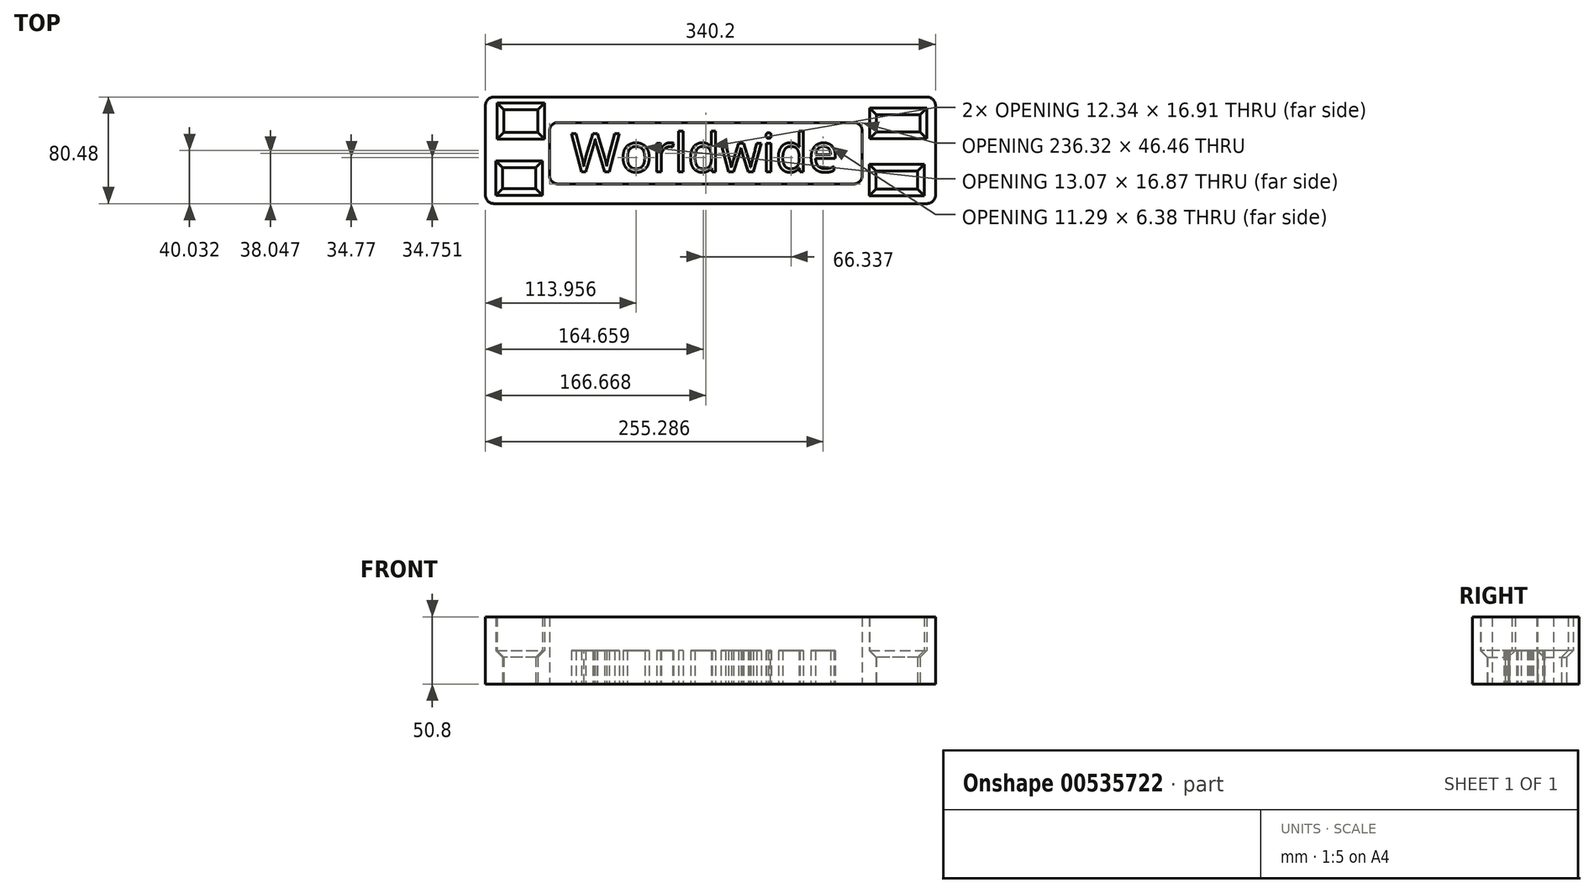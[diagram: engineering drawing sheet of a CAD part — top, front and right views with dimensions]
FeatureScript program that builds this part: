
annotation { "Feature Type Name" : "Feature", "Feature Type Description" : "" }
export const myFeature = defineFeature(function(context is Context, id is Id, definition is map)
    precondition{}
    {
        {
            var Q0;
            Q0=qCreatedBy(makeId("Top.planeOp"),FACE);
            var sketch = newSketch(context, id + "F0", { "sketchPlane" : qUnion([Q0])});
            skLineSegment(sketch, "E0.bottom", {"start": v(-163.75, 40.24) * mm, "end": v(163.75, 40.24) * mm});
            skLineSegment(sketch, "E0.top", {"start": v(-163.75, -40.24) * mm, "end": v(163.75, -40.24) * mm});
            skLineSegment(sketch, "E0.left", {"start": v(-170.1, 33.9) * mm, "end": v(-170.1, -33.9) * mm});
            skLineSegment(sketch, "E0.right", {"start": v(170.1, 33.9) * mm, "end": v(170.1, -33.9) * mm});
            skPoint(sketch, "E0.middle", {"position": v(0, 0) * mm});
            skPoint(sketch, "E1.visualSharp", {"position": v(-170.1, 40.24) * mm});
            skArc(sketch, "E1.filletArc", {"start": v(-163.75, 40.24) * mm, "mid": v(-168.24, 38.38) * mm, "end": v(-170.1, 33.9) * mm});
            skPoint(sketch, "E2.visualSharp", {"position": v(170.1, 40.24) * mm});
            skArc(sketch, "E2.filletArc", {"start": v(170.1, 33.9) * mm, "mid": v(168.24, 38.38) * mm, "end": v(163.75, 40.24) * mm});
            skPoint(sketch, "E3.visualSharp", {"position": v(-170.1, -40.24) * mm});
            skArc(sketch, "E3.filletArc", {"start": v(-170.1, -33.9) * mm, "mid": v(-168.24, -38.38) * mm, "end": v(-163.75, -40.24) * mm});
            skPoint(sketch, "E4.visualSharp", {"position": v(170.1, -40.24) * mm});
            skArc(sketch, "E4.filletArc", {"start": v(163.75, -40.24) * mm, "mid": v(168.24, -38.38) * mm, "end": v(170.1, -33.9) * mm});
            skLineSegment(sketch, "E5.bottom", {"start": v(0, 0) * mm, "end": v(0, 0) * mm});
            skLineSegment(sketch, "E5.top", {"start": v(0, 0) * mm, "end": v(0, 0) * mm});
            skLineSegment(sketch, "E5.left", {"start": v(0, 0) * mm, "end": v(0, 0) * mm});
            skLineSegment(sketch, "E5.right", {"start": v(0, 0) * mm, "end": v(0, 0) * mm});
            skLineSegment(sketch, "E6.bottom", {"start": v(108.38, 21.04) * mm, "end": v(-115.24, 21.04) * mm});
            skLineSegment(sketch, "E6.top", {"start": v(108.38, -25.42) * mm, "end": v(-115.24, -25.42) * mm});
            skLineSegment(sketch, "E6.left", {"start": v(114.73, 14.69) * mm, "end": v(114.73, -19.07) * mm});
            skLineSegment(sketch, "E6.right", {"start": v(-121.59, 14.69) * mm, "end": v(-121.59, -19.07) * mm});
            skPoint(sketch, "E7.visualSharp", {"position": v(114.73, 21.04) * mm});
            skArc(sketch, "E7.filletArc", {"start": v(114.73, 14.69) * mm, "mid": v(112.87, 19.18) * mm, "end": v(108.38, 21.04) * mm});
            skPoint(sketch, "E8.visualSharp", {"position": v(114.73, -25.42) * mm});
            skArc(sketch, "E8.filletArc", {"start": v(108.38, -25.42) * mm, "mid": v(112.87, -23.56) * mm, "end": v(114.73, -19.07) * mm});
            skPoint(sketch, "E9.visualSharp", {"position": v(-121.59, 21.04) * mm});
            skArc(sketch, "E9.filletArc", {"start": v(-115.24, 21.04) * mm, "mid": v(-119.73, 19.18) * mm, "end": v(-121.59, 14.69) * mm});
            skPoint(sketch, "E10.visualSharp", {"position": v(-121.59, -25.42) * mm});
            skArc(sketch, "E10.filletArc", {"start": v(-121.59, -19.07) * mm, "mid": v(-119.73, -23.56) * mm, "end": v(-115.24, -25.42) * mm});
            skLineSegment(sketch, "E11.bottom", {"start": v(158.53, 26.97) * mm, "end": v(125.6, 26.97) * mm});
            skLineSegment(sketch, "E11.top", {"start": v(158.53, 14.03) * mm, "end": v(125.6, 14.03) * mm});
            skLineSegment(sketch, "E11.left", {"start": v(158.53, 26.97) * mm, "end": v(158.53, 14.03) * mm});
            skLineSegment(sketch, "E11.right", {"start": v(125.6, 26.97) * mm, "end": v(125.6, 14.03) * mm});
            skLineSegment(sketch, "E12.bottom", {"start": v(156.44, -15.5) * mm, "end": v(125.26, -15.5) * mm});
            skLineSegment(sketch, "E12.top", {"start": v(156.44, -29.19) * mm, "end": v(125.26, -29.19) * mm});
            skLineSegment(sketch, "E12.left", {"start": v(156.44, -15.5) * mm, "end": v(156.44, -29.19) * mm});
            skLineSegment(sketch, "E12.right", {"start": v(125.26, -15.5) * mm, "end": v(125.26, -29.19) * mm});
            skLineSegment(sketch, "E13.bottom", {"start": v(-130.34, 30.8) * mm, "end": v(-156.01, 30.8) * mm});
            skLineSegment(sketch, "E13.top", {"start": v(-130.34, 13.47) * mm, "end": v(-156.01, 13.47) * mm});
            skLineSegment(sketch, "E13.left", {"start": v(-130.34, 30.8) * mm, "end": v(-130.34, 13.47) * mm});
            skLineSegment(sketch, "E13.right", {"start": v(-156.01, 30.8) * mm, "end": v(-156.01, 13.47) * mm});
            skLineSegment(sketch, "E14.bottom", {"start": v(-132.05, -13.2) * mm, "end": v(-157.2, -13.2) * mm});
            skLineSegment(sketch, "E14.top", {"start": v(-132.05, -28.96) * mm, "end": v(-157.2, -28.96) * mm});
            skLineSegment(sketch, "E14.left", {"start": v(-132.05, -13.2) * mm, "end": v(-132.05, -28.96) * mm});
            skLineSegment(sketch, "E14.right", {"start": v(-157.2, -13.2) * mm, "end": v(-157.2, -28.96) * mm});
            skLineSegment(sketch, "E15.bottom", {"start": v(-143.18, 30.8) * mm, "end": v(-143.18, 30.8) * mm});
            skLineSegment(sketch, "E15.top", {"start": v(-143.18, 30.8) * mm, "end": v(-143.18, 30.8) * mm});
            skLineSegment(sketch, "E15.left", {"start": v(-143.18, 30.8) * mm, "end": v(-143.18, 30.8) * mm});
            skLineSegment(sketch, "E15.right", {"start": v(-143.18, 30.8) * mm, "end": v(-143.18, 30.8) * mm});
            skText(sketch, "E16", { "text": "worldwide", "fontName": "OpenSans-Regular.ttf"});
            const initialGuessF0  = {"E16": [-0.1022, -0.01723, 1, 0, 0.01723]};
            skSetInitialGuess(sketch, initialGuessF0);
            skSolve(sketch);
        }
        {
            var Q0;
            Q0 = qSketchRegion(id + "F0", true);
            var Q1;
            Q1=makeQuery(id+"F0.imprint","IMPRINT",FACE,{"disambiguationData":[TD([[makeQuery(id+"F0.imprint","IMPRINT",EDGE,{"derivedFrom":sQuery(id+"F0.wireOp",EDGE,"E0.bottom")}),-1.0]])]});
            extrude(context, id + "F1", {"entities" : qUnion([Q0, Q1]), "depth" : 25.4 * mm, "offsetDistance" : 25.4 * mm});
        }
        {
            var Q0;
            Q0=makeQuery(id+"F1.opExtrude","CAP_EDGE",EDGE,{"disambiguationData":[OSD([sQuery(id+"F0.wireOp",EDGE,"E11.top")])],"isStart":false});
            var Q1;
            Q1=makeQuery(id+"F1.opExtrude","CAP_EDGE",EDGE,{"disambiguationData":[OSD([sQuery(id+"F0.wireOp",EDGE,"E11.bottom")])],"isStart":false});
            var Q2;
            Q2=makeQuery(id+"F1.opExtrude","CAP_EDGE",EDGE,{"disambiguationData":[OSD([sQuery(id+"F0.wireOp",EDGE,"E11.right")])],"isStart":false});
            var Q3;
            Q3=makeQuery(id+"F1.opExtrude","CAP_EDGE",EDGE,{"disambiguationData":[OSD([sQuery(id+"F0.wireOp",EDGE,"E11.left")])],"isStart":false});
            var Q4;
            Q4=makeQuery(id+"F1.opExtrude","CAP_EDGE",EDGE,{"disambiguationData":[OSD([sQuery(id+"F0.wireOp",EDGE,"E12.bottom")])],"isStart":false});
            var Q5;
            Q5=makeQuery(id+"F1.opExtrude","CAP_EDGE",EDGE,{"disambiguationData":[OSD([sQuery(id+"F0.wireOp",EDGE,"E12.top")])],"isStart":false});
            var Q6;
            Q6=makeQuery(id+"F1.opExtrude","CAP_EDGE",EDGE,{"disambiguationData":[OSD([sQuery(id+"F0.wireOp",EDGE,"E12.left")])],"isStart":false});
            var Q7;
            Q7=makeQuery(id+"F1.opExtrude","CAP_EDGE",EDGE,{"disambiguationData":[OSD([sQuery(id+"F0.wireOp",EDGE,"E12.right")])],"isStart":false});
            var Q8;
            Q8=makeQuery(id+"F1.opExtrude","CAP_EDGE",EDGE,{"disambiguationData":[OSD([sQuery(id+"F0.wireOp",EDGE,"E13.bottom")])],"isStart":false});
            var Q9;
            Q9=makeQuery(id+"F1.opExtrude","CAP_EDGE",EDGE,{"disambiguationData":[OSD([sQuery(id+"F0.wireOp",EDGE,"E13.left")])],"isStart":false});
            var Q10;
            Q10=makeQuery(id+"F1.opExtrude","CAP_EDGE",EDGE,{"disambiguationData":[OSD([sQuery(id+"F0.wireOp",EDGE,"E13.right")])],"isStart":false});
            var Q11;
            Q11=makeQuery(id+"F1.opExtrude","CAP_EDGE",EDGE,{"disambiguationData":[OSD([sQuery(id+"F0.wireOp",EDGE,"E13.top")])],"isStart":false});
            var Q12;
            Q12=makeQuery(id+"F1.opExtrude","CAP_EDGE",EDGE,{"disambiguationData":[OSD([sQuery(id+"F0.wireOp",EDGE,"E14.bottom")])],"isStart":false});
            var Q13;
            Q13=makeQuery(id+"F1.opExtrude","CAP_EDGE",EDGE,{"disambiguationData":[OSD([sQuery(id+"F0.wireOp",EDGE,"E14.right")])],"isStart":false});
            var Q14;
            Q14=makeQuery(id+"F1.opExtrude","CAP_EDGE",EDGE,{"disambiguationData":[OSD([sQuery(id+"F0.wireOp",EDGE,"E14.top")])],"isStart":false});
            var Q15;
            Q15=makeQuery(id+"F1.opExtrude","CAP_EDGE",EDGE,{"disambiguationData":[OSD([sQuery(id+"F0.wireOp",EDGE,"E14.left")])],"isStart":false});
            chamfer(context, id + "F2", {"entities" : qUnion([Q0, Q1, Q2, Q3, Q4, Q5, Q6, Q7, Q8, Q9, Q10, Q11, Q12, Q13, Q14, Q15]), "width" : 5.08 * mm, "tangentPropagation" : true});
        }
        {
            var Q0;
            Q0=qCreatedBy(makeId("Top.planeOp"),FACE);
            var sketch = newSketch(context, id + "F3", { "sketchPlane" : qUnion([Q0])});
            skText(sketch, "E17", { "text": "Worldwide", "fontName": "OpenSans-Regular.ttf"});
            const initialGuessF3  = {"E17": [-0.1057, -0.01627, 1, 0, 0.02906]};
            skSetInitialGuess(sketch, initialGuessF3);
            skSolve(sketch);
        }
        {
            var Q0;
            Q0 = qSketchRegion(id + "F3", true);
            extrude(context, id + "F4", {"entities" : qUnion([Q0]), "depth" : 25.4 * mm, "offsetDistance" : 25.4 * mm});
        }
        {
            var Q0;
            Q0=makeQuery(id+"F1.opExtrude","CAP_FACE",FACE,{"disambiguationData":[OSD([sQuery(id+"F0.wireOp",EDGE,"E0.bottom"),sQuery(id+"F0.wireOp",EDGE,"E0.top"),sQuery(id+"F0.wireOp",EDGE,"E0.left"),sQuery(id+"F0.wireOp",EDGE,"E0.right"),sQuery(id+"F0.wireOp",EDGE,"E1.filletArc"),sQuery(id+"F0.wireOp",EDGE,"E2.filletArc"),sQuery(id+"F0.wireOp",EDGE,"E3.filletArc"),sQuery(id+"F0.wireOp",EDGE,"E4.filletArc"),sQuery(id+"F0.wireOp",EDGE,"E6.bottom"),sQuery(id+"F0.wireOp",EDGE,"E6.top"),sQuery(id+"F0.wireOp",EDGE,"E6.left"),sQuery(id+"F0.wireOp",EDGE,"E6.right"),sQuery(id+"F0.wireOp",EDGE,"E7.filletArc"),sQuery(id+"F0.wireOp",EDGE,"E8.filletArc"),sQuery(id+"F0.wireOp",EDGE,"E9.filletArc"),sQuery(id+"F0.wireOp",EDGE,"E10.filletArc"),sQuery(id+"F0.wireOp",EDGE,"E11.bottom"),sQuery(id+"F0.wireOp",EDGE,"E11.top"),sQuery(id+"F0.wireOp",EDGE,"E11.left"),sQuery(id+"F0.wireOp",EDGE,"E11.right"),sQuery(id+"F0.wireOp",EDGE,"E12.bottom"),sQuery(id+"F0.wireOp",EDGE,"E12.top"),sQuery(id+"F0.wireOp",EDGE,"E12.left"),sQuery(id+"F0.wireOp",EDGE,"E12.right"),sQuery(id+"F0.wireOp",EDGE,"E13.bottom"),sQuery(id+"F0.wireOp",EDGE,"E13.top"),sQuery(id+"F0.wireOp",EDGE,"E13.left"),sQuery(id+"F0.wireOp",EDGE,"E13.right"),sQuery(id+"F0.wireOp",EDGE,"E14.bottom"),sQuery(id+"F0.wireOp",EDGE,"E14.top"),sQuery(id+"F0.wireOp",EDGE,"E14.left"),sQuery(id+"F0.wireOp",EDGE,"E14.right")])],"isStart":false});
            extrude(context, id + "F5", {"entities" : qUnion([Q0]), "operationType" : NewBodyOperationType.ADD, "depth" : 25.4 * mm, "offsetDistance" : 25.4 * mm});
        }
    });
